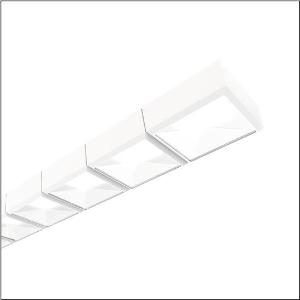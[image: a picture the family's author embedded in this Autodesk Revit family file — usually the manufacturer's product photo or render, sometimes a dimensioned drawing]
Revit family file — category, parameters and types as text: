
# Revit family: scriptus_r__11_5mz212d04wa_64be
name_source: partatom
category: Lighting Fixtures
units: mm (PartAtom-declared; Revit-internal decimal feet)

## family parameters
Cut with Voids When Loaded = No
Host = Face
Light Source = No
Part Type = Normal
Room Calculation Point = No
Round Connector Dimension = Use Diameter
Shared = No

## types (1)
- Scriptus® 11 (1 x LED 4000K / CRI = 80 (unbekannt), 2410 lm, 4000K)
    Apparent Load = 35 VA
    CIE Flux Codes = 82 95 99 100 100
    Color Rendering = 80
    Color Temperature = 4000K
    Default Elevation = 1800 mm
    Description = Scriptus® 11, office luminaire, primary optical cover: lenses, CAT 2 (L<= 3000cd/m²), light emission: direct distribution, primary light characteristic: symmetric, installation type: surface-mounted, LED, rated luminous flux: 4.810lm, luminous efficacy: 139lm/W, light colour: 840, colour temperature: 4000K, control gear: ECG DALI, with terminal, 5-pole, mains connection: 230V, AC, 50Hz, rated input power: 35W, housing, luminaire housing, of aluminium, traffic white (RAL 9016), length: 1.658mm, width: 114mm, height: 57mm, protection rating (complete): IP20, insulation class (complete): insulation class I (protective earthing), certification: CE, ENEC, VDE, protection symbol: F, permissible operating ambient temperature: 0..+35°C, standard: EN 50419, packaging unit: 1 piece
    Height = 57 mm
    Lamp = 1 x LED 4000K / CRI >= 80 (unbekannt)
    Lamp Light Flux = 2410 lm
    Lamp count = 1
    Length = 1658 mm
    Luminous efficacy = 139 lm/W
    Manufacturer = Siteco
    ModVariant = No
    Model = 5MZ212D04WA
    Mounting Place = Ceiling
    Mounting Type = Surface mounted
    Number of Poles = 1
    OnlyDefault = Yes
    Power Factor = 1
    Product Name = Scriptus® 11
    Product group = office luminaire | ceiling mounted
    ProductGroupID = 300
    Protection Class = Protection class I
    Protection Degree = IP 20
    RLX_Detail_Level = 1
    RLX_Emergency_Light_Flux = 0 lm
    RLX_Emergency_Type = 0
    RLX_Emergency_Type_DB = No
    RlxData = <blob elided: 29501 chars, md5=8341451f>
    Socket = socket
    Standby Power = 0 W
    System Light Flux = 4820 lm
    System Power = 35 W
    Type Comments = Product without accessories
    Type Image = l_1004833.jpg
    URL = http://relux.com
    VarID = ---
    Voltage = 0 V
    Weight = 0.00 kg
    Width = 114 mm

## geometry (parser evidence)
native form markers: Blend x4, Sweep x15
no freeform markers — native parametric forms only
